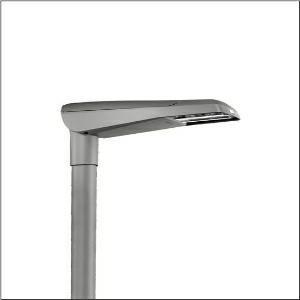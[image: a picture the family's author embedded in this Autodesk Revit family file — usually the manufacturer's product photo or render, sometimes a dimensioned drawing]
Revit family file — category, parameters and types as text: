
# Revit family: streetlight_sl_11_iq_micro___st0_5a_5xc1b41f08ce_e569
name_source: partatom
category: Lighting Fixtures
units: mm (PartAtom-declared; Revit-internal decimal feet)

## family parameters
Cut with Voids When Loaded = No
Host = Face
Light Source = No
Part Type = Normal
Room Calculation Point = No
Round Connector Dimension = Use Diameter
Shared = No

## types (1)
- --- (1 x LED, 1940 lm, 12.6 W, 4000K)
    Apparent Load = 13 VA
    CIE Flux Codes = 42 72 97 100 100
    Color Rendering = 70
    Color Temperature = 4000K
    Default Elevation = 1800 mm
    Description = Streetlight SL 11 iQ micro, mast luminaire, primary light control with 3 zone facetted reflector, of plastic, silver coated, highly specular, primary optical cover: cover, of PMMA, transparent, light distribution: ST0.5a, light emission: direct distribution, primary light characteristic: asymmetric, installation type: post-top, side-entry, lamps: LED, High Power LED, rated values: 1.940lm | 12,6W | 154lm/W (begin service life); end service life: 1.940lm | 12,9W; at 50% lumin. flux: 970lm | 6,8W | 142,6lm/W, colour temperature: 4000K, colour rendering: CRI > 70, light colour: 740, light setting 1 begin service life: 100% | 1.940lm | 12,6W | 154lm/W | 4.000K, light setting 1 end service life: 12,9W, further light settings possible, control: Street-Remote, optimised constant luminous flux control (CLO 2.0), Desk-Remote (wireless, voltage-free reading and setting of iQ features in the workshop via application-optimized NFC function/RFID function), Light-Fading, Smart-Wire, Night-Set, Lumen-Switch, Temp-Guard, Auto-Match, with cable H07RN-F 3x 1.5mm², mains connection: 230..240V, AC, 50/60Hz, connection cable pre-assembled, cable length: 5,5m, luminaire housing, of diecast aluminium, powder-coated, SITECO metallic grey (DB 702S), please order mast flange separately, inclination adjustable without tools: 0°, 5°, 10°, 15° (post-top) | 0°, -5°, -10°, -15° (side-entry), sealing non-destructively replaceable, multi-level sealing system, length: 600mm, width: 174mm, height: 116mm, mast flange for spigot size: 42mm (side-entry): 5XC10008XM4, 60/48mm (side-entry/post-top): 5XC10108XM2, 76/60mm (side-entry/post-top): 5XC10108XM1, equipment: standard, protection rating (complete): IP66, insulation class (complete): insulation class II (safety insulation), certification: CE, ENEC, ENEC+, VDE, impact resistance: IK10, permissible operating ambient temperature for outdoor applications: -25..+50°C, standard-compliant lighting for roads and squares, Environmental Product Declaration (EPD) tested and certified by an independent institute, packaging unit: 1 piece

Light Distribution: ST0.5a
    Height = 116 mm
    Lamp = 1 x LED
    Lamp Light Flux = 1940 lm
    Lamp Power = 12.6 W
    Lamp count = 1
    Length = 600 mm
    Luminous efficacy = 154 lm/W
    Manufacturer = Siteco
    ModVariant = No
    Model = 5XC1B41F08CE
    Number of Poles = 1
    OnlyDefault = Yes
    Power Factor = 1
    Product Name = Streetlight SL 11 iQ micro | ST0.5a
    Product group = mast luminaire | pylon top
    ProductGroupID = 6100
    Protection Class = Protection class II
    Protection Degree = IP 66
    RLX_Detail_Level = 1
    RLX_Emergency_Light_Flux = 0 lm
    RLX_Emergency_Type = 0
    RLX_Emergency_Type_DB = No
    RlxData = <blob elided: 26741 chars, md5=e14a6966>
    Socket = socket
    Standby Power = 0 W
    System Light Flux = 1940 lm
    System Power = 13 W
    Type Comments = factory setting: luminous flux: 100 % | dim-lin: 254 | 229 mA
    Type Image = l_1006566.jpg
    URL = http://relux.com
    VarID = @adj_021819
    Voltage = 0 V
    Weight = 0.00 kg
    Width = 174 mm

## geometry (parser evidence)
native form markers: Blend x4, Sweep x10
no freeform markers — native parametric forms only
